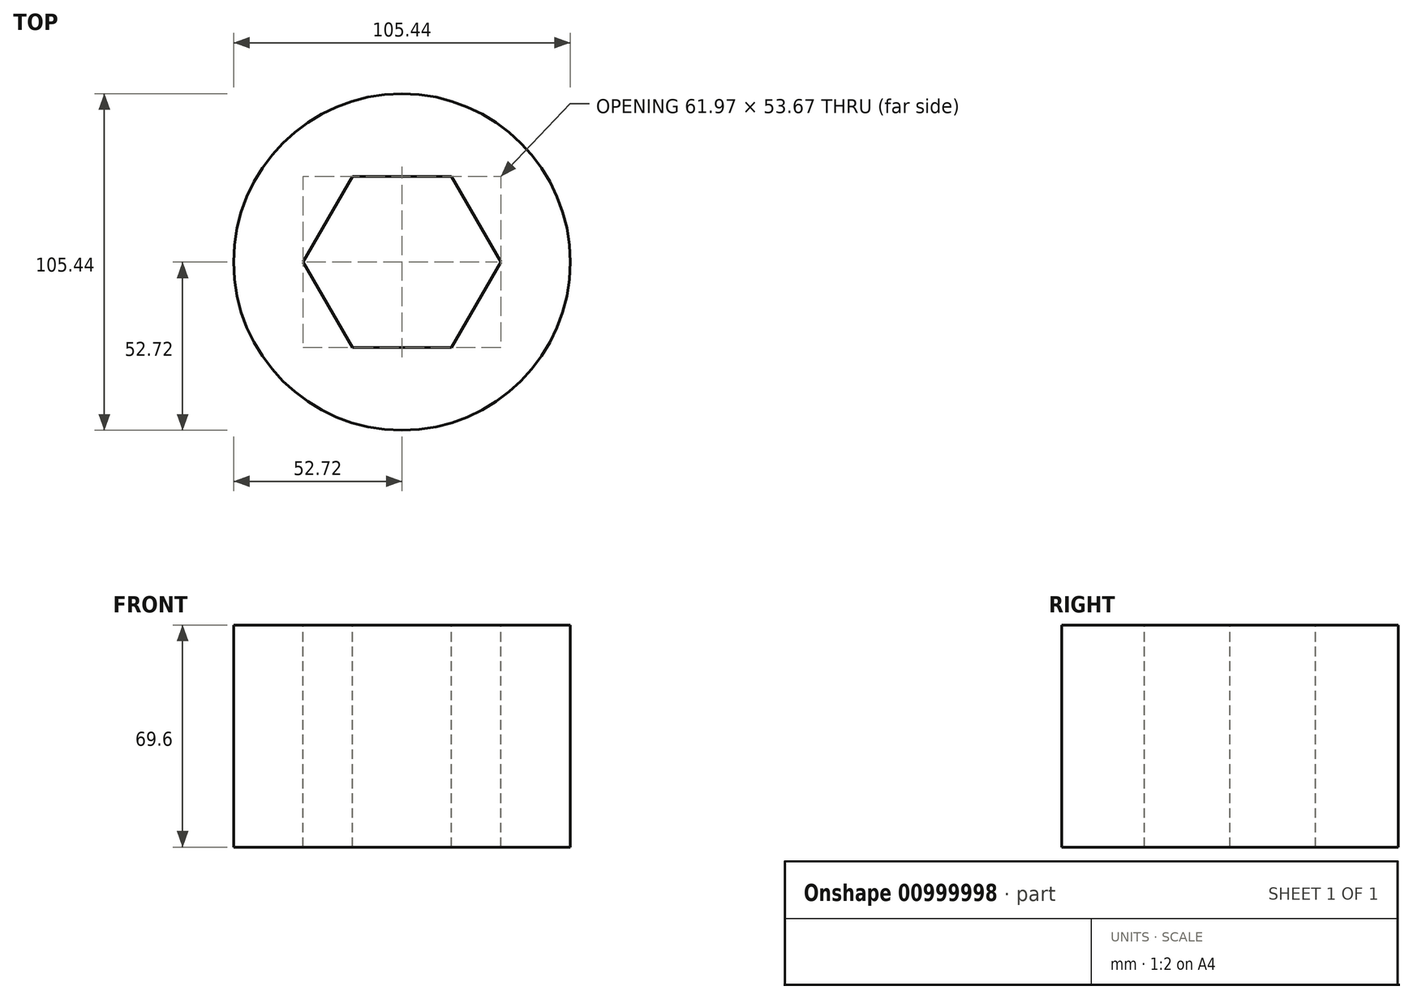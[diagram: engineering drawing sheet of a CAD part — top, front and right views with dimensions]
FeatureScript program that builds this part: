
annotation { "Feature Type Name" : "Feature", "Feature Type Description" : "" }
export const myFeature = defineFeature(function(context is Context, id is Id, definition is map)
    precondition{}
    {
        {
            var Q0;
            Q0=qCreatedBy(makeId("Top.planeOp"),FACE);
            var sketch = newSketch(context, id + "F0", { "sketchPlane" : qUnion([Q0])});
            skCircle(sketch, "E0", {"center": v(0, 0) * mm, "radius": 52.72 * mm});
            skSolve(sketch);
        }
        {
            var Q0;
            Q0=makeQuery(id+"F0.imprint","IMPRINT",FACE,{"disambiguationData":[TD([[makeQuery(id+"F0.imprint","IMPRINT",EDGE,{"derivedFrom":sQuery(id+"F0.wireOp",EDGE,"E0")}),1.0]])]});
            extrude(context, id + "F1", {"entities" : qUnion([Q0]), "depth" : 69.6 * mm, "offsetDistance" : 25.4 * mm});
        }
        {
            var Q0;
            Q0=makeQuery(id+"F1.opExtrude","CAP_FACE",FACE,{"disambiguationData":[OSD([sQuery(id+"F0.wireOp",EDGE,"E0")])],"isStart":false});
            var sketch = newSketch(context, id + "F2", { "sketchPlane" : qUnion([Q0])});
            skSolve(sketch);
        }
        {
            var Q0;
            Q0=makeQuery(id+"F2.imprint","IMPRINT",FACE,{"disambiguationData":[TD([[makeQuery(id+"F2.imprint","IMPRINT",EDGE,{"derivedFrom":makeQuery(id+"F1.opExtrude","CAP_EDGE",EDGE,{"disambiguationData":[OSD([sQuery(id+"F0.wireOp",EDGE,"E0")])],"isStart":false})}),1.0]])]});
            var sketch = newSketch(context, id + "F3", { "sketchPlane" : qUnion([Q0])});
            skCircle(sketch, "E1.cCircle", {"center": v(0, 0) * mm, "radius": 26.83 * mm, "construction": true});
            skLineSegment(sketch, "E1.0", {"start": v(-15.5, 26.83) * mm, "end": v(15.5, 26.83) * mm});
            skLineSegment(sketch, "E1.1", {"start": v(15.5, 26.83) * mm, "end": v(30.98, 0) * mm});
            skLineSegment(sketch, "E1.2", {"start": v(30.98, 0) * mm, "end": v(15.5, -26.83) * mm});
            skLineSegment(sketch, "E1.3", {"start": v(15.5, -26.83) * mm, "end": v(-15.5, -26.83) * mm});
            skLineSegment(sketch, "E1.4", {"start": v(-15.5, -26.83) * mm, "end": v(-30.98, 0) * mm});
            skLineSegment(sketch, "E1.5", {"start": v(-30.98, 0) * mm, "end": v(-15.5, 26.83) * mm});
            skPoint(sketch, "E1.0.midPoint", {"position": v(0, 26.83) * mm});
            skSolve(sketch);
        }
        {
            var Q0;
            Q0=makeQuery(id+"F3.imprint","IMPRINT",FACE,{"disambiguationData":[TD([[makeQuery(id+"F3.imprint","IMPRINT",EDGE,{"derivedFrom":sQuery(id+"F3.wireOp",EDGE,"E1.0")}),-1.0]])]});
            extrude(context, id + "F4", {"entities" : qUnion([Q0]), "operationType" : NewBodyOperationType.REMOVE, "oppositeDirection" : true, "depth" : 127.76 * mm, "offsetDistance" : 25.4 * mm});
        }
    });
